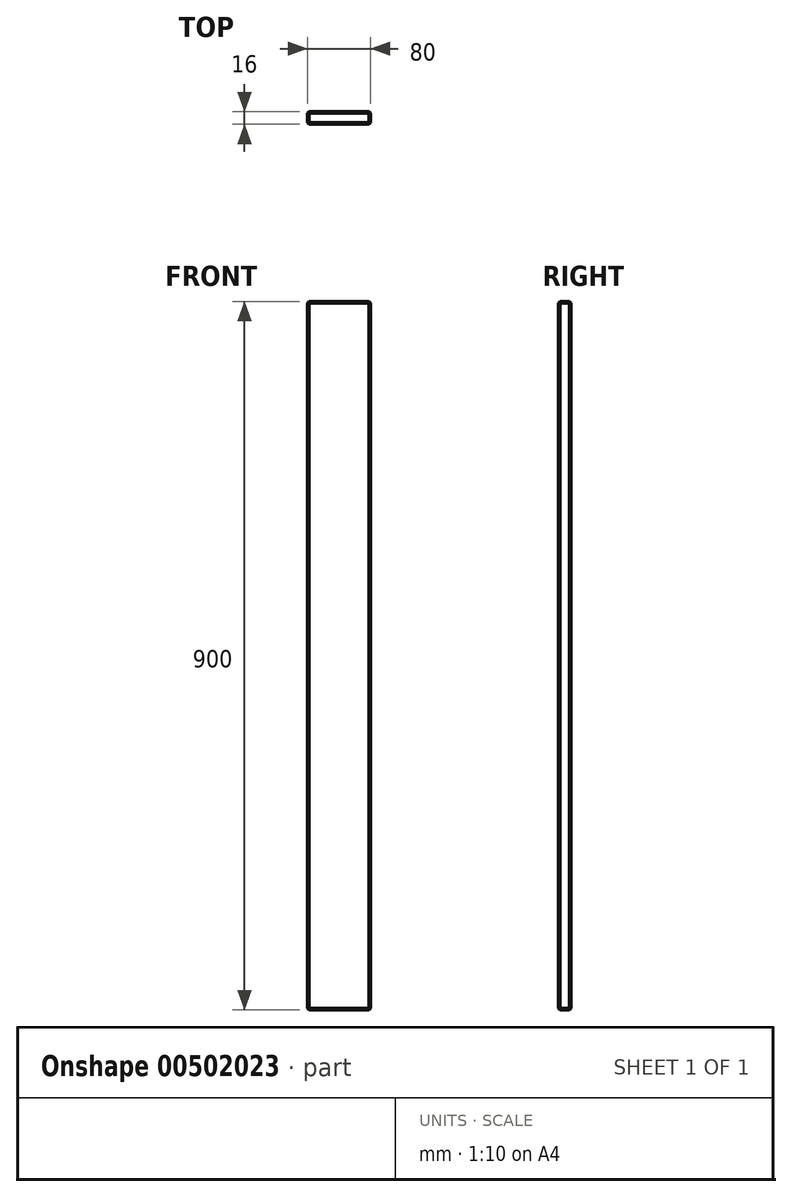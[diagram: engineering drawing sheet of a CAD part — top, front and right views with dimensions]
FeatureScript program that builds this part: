
annotation { "Feature Type Name" : "Feature", "Feature Type Description" : "" }
export const myFeature = defineFeature(function(context is Context, id is Id, definition is map)
    precondition{}
    {
        {
            var Q0;
            Q0=qCreatedBy(makeId("Front.planeOp"),FACE);
            var sketch = newSketch(context, id + "F0", { "sketchPlane" : qUnion([Q0])});
            skLineSegment(sketch, "E0.bottom", {"start": v(-40, 450) * mm, "end": v(40, 450) * mm});
            skLineSegment(sketch, "E0.top", {"start": v(-40, -450) * mm, "end": v(40, -450) * mm});
            skLineSegment(sketch, "E0.left", {"start": v(-40, 450) * mm, "end": v(-40, -450) * mm});
            skLineSegment(sketch, "E0.right", {"start": v(40, 450) * mm, "end": v(40, -450) * mm});
            skSolve(sketch);
        }
        {
            var Q0;
            Q0 = qSketchRegion(id + "F0", true);
            extrude(context, id + "F1", {"entities" : qUnion([Q0]), "depth" : 16 * mm, "offsetDistance" : 25 * mm});
        }
        {
            var Q0;
            Q0=makeQuery(id+"F1.opExtrude","CAP_EDGE",EDGE,{"disambiguationData":[OSD([sQuery(id+"F0.wireOp",EDGE,"E0.top")])],"isStart":false});
            var Q1;
            Q1=makeQuery(id+"F1.opExtrude","CAP_EDGE",EDGE,{"disambiguationData":[OSD([sQuery(id+"F0.wireOp",EDGE,"E0.right")])],"isStart":false});
            var Q2;
            Q2=makeQuery(id+"F1.opExtrude","SWEPT_EDGE",EDGE,{"disambiguationData":[OSD([sQuery(id+"F0.wireOp",EDGE,"E0.top"),sQuery(id+"F0.wireOp",EDGE,"E0.right")])]});
            var Q3;
            Q3=makeQuery(id+"F1.opExtrude","CAP_EDGE",EDGE,{"disambiguationData":[OSD([sQuery(id+"F0.wireOp",EDGE,"E0.right")])],"isStart":true});
            var Q4;
            Q4=makeQuery(id+"F1.opExtrude","CAP_EDGE",EDGE,{"disambiguationData":[OSD([sQuery(id+"F0.wireOp",EDGE,"E0.top")])],"isStart":true});
            var Q5;
            Q5=makeQuery(id+"F1.opExtrude","SWEPT_EDGE",EDGE,{"disambiguationData":[OSD([sQuery(id+"F0.wireOp",EDGE,"E0.top"),sQuery(id+"F0.wireOp",EDGE,"E0.left")])]});
            var Q6;
            Q6=makeQuery(id+"F1.opExtrude","CAP_EDGE",EDGE,{"disambiguationData":[OSD([sQuery(id+"F0.wireOp",EDGE,"E0.left")])],"isStart":true});
            var Q7;
            Q7=makeQuery(id+"F1.opExtrude","CAP_EDGE",EDGE,{"disambiguationData":[OSD([sQuery(id+"F0.wireOp",EDGE,"E0.left")])],"isStart":false});
            var Q8;
            Q8=makeQuery(id+"F1.opExtrude","SWEPT_EDGE",EDGE,{"disambiguationData":[OSD([sQuery(id+"F0.wireOp",EDGE,"E0.bottom"),sQuery(id+"F0.wireOp",EDGE,"E0.left")])]});
            var Q9;
            Q9=makeQuery(id+"F1.opExtrude","CAP_EDGE",EDGE,{"disambiguationData":[OSD([sQuery(id+"F0.wireOp",EDGE,"E0.bottom")])],"isStart":false});
            var Q10;
            Q10=makeQuery(id+"F1.opExtrude","CAP_EDGE",EDGE,{"disambiguationData":[OSD([sQuery(id+"F0.wireOp",EDGE,"E0.bottom")])],"isStart":true});
            var Q11;
            Q11=makeQuery(id+"F1.opExtrude","SWEPT_EDGE",EDGE,{"disambiguationData":[OSD([sQuery(id+"F0.wireOp",EDGE,"E0.bottom"),sQuery(id+"F0.wireOp",EDGE,"E0.right")])]});
            chamfer(context, id + "F2", {"entities" : qUnion([Q0, Q1, Q2, Q3, Q4, Q5, Q6, Q7, Q8, Q9, Q10, Q11]), "width" : 2 * mm, "tangentPropagation" : true});
        }
    });
